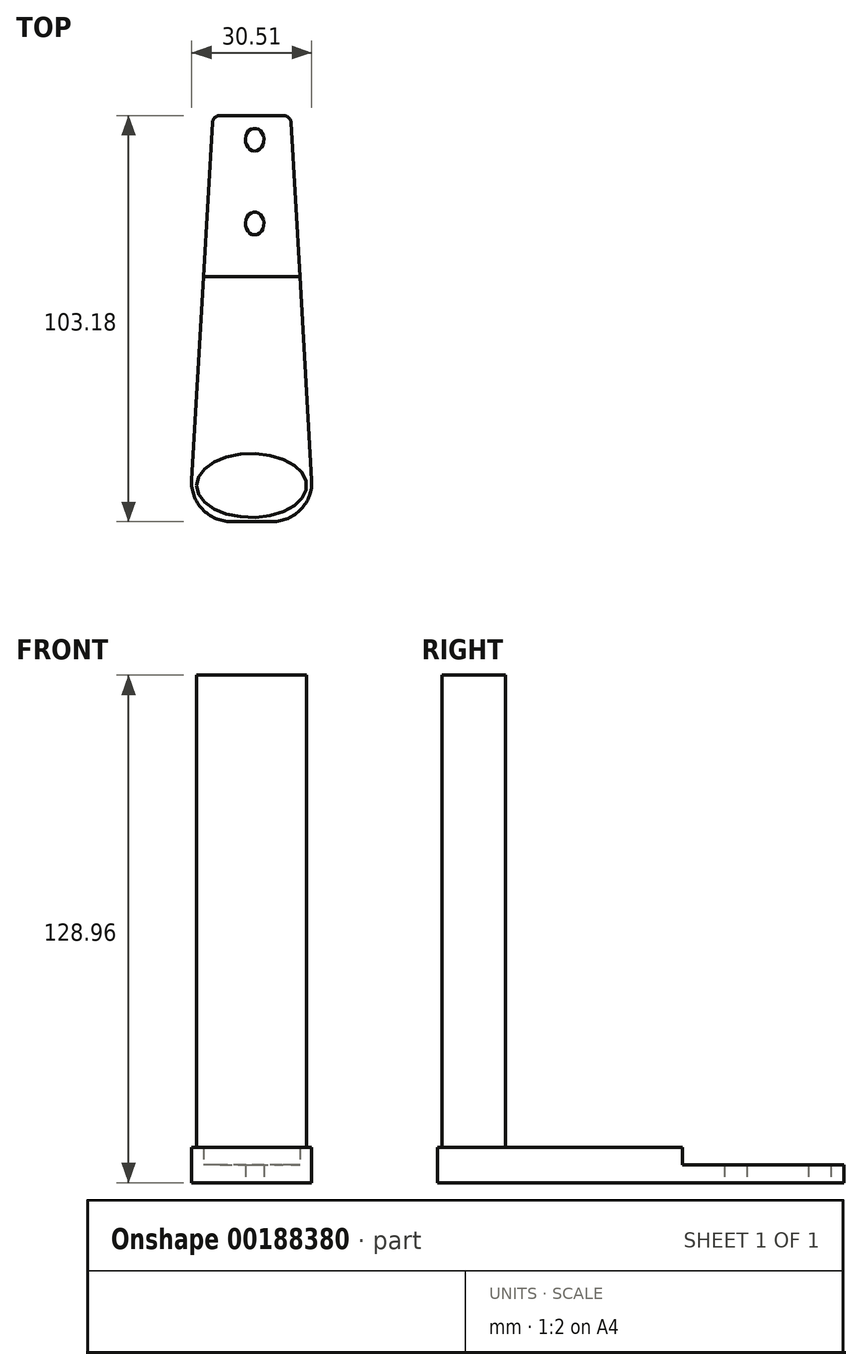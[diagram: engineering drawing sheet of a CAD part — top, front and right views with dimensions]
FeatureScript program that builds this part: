
annotation { "Feature Type Name" : "Feature", "Feature Type Description" : "" }
export const myFeature = defineFeature(function(context is Context, id is Id, definition is map)
    precondition{}
    {
        {
            var Q0;
            Q0=qCreatedBy(makeId("Top.planeOp"),FACE);
            var sketch = newSketch(context, id + "F0", { "sketchPlane" : qUnion([Q0])});
            skLineSegment(sketch, "E0", {"start": v(-8.74, 43.4) * mm, "end": v(7.26, 43.4) * mm});
            skLineSegment(sketch, "E1", {"start": v(-16.6, -59.78) * mm, "end": v(15.1, -59.78) * mm});
            skLineSegment(sketch, "E2", {"start": v(9.26, 41.52) * mm, "end": v(15.1, -59.78) * mm});
            skLineSegment(sketch, "E3", {"start": v(-10.74, 41.52) * mm, "end": v(-16.6, -59.78) * mm});
            skEllipse(sketch, "E4", {"center": v(0, 37.26) * mm, "majorRadius": 2.87 * mm, "minorRadius": 2.37 * mm, "majorAxis": v(0, -1)});
            skEllipse(sketch, "E5", {"center": v(0, 15.95) * mm, "majorRadius": 2.87 * mm, "minorRadius": 2.37 * mm, "majorAxis": v(0, -1)});
            skPoint(sketch, "E6.visualSharp", {"position": v(-10.63, 43.4) * mm});
            skArc(sketch, "E6.filletArc", {"start": v(-8.74, 43.4) * mm, "mid": v(-10.12, 42.86) * mm, "end": v(-10.74, 41.52) * mm});
            skPoint(sketch, "E7.visualSharp", {"position": v(9.15, 43.4) * mm});
            skArc(sketch, "E7.filletArc", {"start": v(9.26, 41.52) * mm, "mid": v(8.63, 42.86) * mm, "end": v(7.26, 43.4) * mm});
            skSolve(sketch);
        }
        {
            var Q0;
            Q0=makeQuery(id+"F0.imprint","IMPRINT",FACE,{"disambiguationData":[TD([[makeQuery(id+"F0.imprint","IMPRINT",EDGE,{"derivedFrom":sQuery(id+"F0.wireOp",EDGE,"E0")}),-1.0]])]});
            extrude(context, id + "F1", {"entities" : qUnion([Q0]), "depth" : 4.5 * mm});
        }
        {
            var Q0;
            Q0=qCreatedBy(makeId("Top.planeOp"),FACE);
            var sketch = newSketch(context, id + "F2", { "sketchPlane" : qUnion([Q0])});
            skLineSegment(sketch, "E8", {"start": v(-13, 2.41) * mm, "end": v(11.52, 2.41) * mm});
            skLineSegment(sketch, "E9", {"start": v(11.52, 2.41) * mm, "end": v(15.1, -59.78) * mm});
            skLineSegment(sketch, "E10", {"start": v(15.1, -59.78) * mm, "end": v(-16.6, -59.78) * mm});
            skLineSegment(sketch, "E11", {"start": v(-16.6, -59.78) * mm, "end": v(-13, 2.41) * mm});
            skSolve(sketch);
        }
        {
            var Q0;
            Q0 = qSketchRegion(id + "F2", true);
            extrude(context, id + "F3", {"entities" : qUnion([Q0]), "operationType" : NewBodyOperationType.ADD, "depth" : 8.96 * mm});
        }
        {
            var Q0;
            Q0=makeQuery(id+"F3.boolean.opBoolean","MERGE",EDGE,{"derivedFrom":[makeQuery(id+"F1.opExtrude","SWEPT_EDGE",EDGE,{"disambiguationData":[OSD([sQuery(id+"F0.wireOp",EDGE,"E1"),sQuery(id+"F0.wireOp",EDGE,"E2")])]}),makeQuery(id+"F3.opExtrude","SWEPT_EDGE",EDGE,{"disambiguationData":[OSD([sQuery(id+"F2.wireOp",EDGE,"E9"),sQuery(id+"F2.wireOp",EDGE,"E10")])]})]});
            fillet(context, id + "F4", {"entities" : qUnion([Q0]), "radius" : 10 * mm, "tangentPropagation" : true, "allowEdgeOverflow" : false});
        }
        {
            var Q0;
            Q0=makeQuery(id+"F3.boolean.opBoolean","MERGE",EDGE,{"derivedFrom":[makeQuery(id+"F1.opExtrude","SWEPT_EDGE",EDGE,{"disambiguationData":[OSD([sQuery(id+"F0.wireOp",EDGE,"E1"),sQuery(id+"F0.wireOp",EDGE,"E3")])]}),makeQuery(id+"F3.opExtrude","SWEPT_EDGE",EDGE,{"disambiguationData":[OSD([sQuery(id+"F2.wireOp",EDGE,"E10"),sQuery(id+"F2.wireOp",EDGE,"E11")])]})]});
            fillet(context, id + "F5", {"entities" : qUnion([Q0]), "radius" : 10 * mm, "tangentPropagation" : true, "allowEdgeOverflow" : false});
        }
        {
            var Q0;
            Q0=makeQuery(id+"F3.opExtrude","CAP_FACE",FACE,{"disambiguationData":[OSD([sQuery(id+"F2.wireOp",EDGE,"E8"),sQuery(id+"F2.wireOp",EDGE,"E9"),sQuery(id+"F2.wireOp",EDGE,"E10"),sQuery(id+"F2.wireOp",EDGE,"E11")])],"isStart":false});
            var sketch = newSketch(context, id + "F6", { "sketchPlane" : qUnion([Q0])});
            skEllipse(sketch, "E12", {"center": v(-0.77, -50.6) * mm, "majorRadius": 14 * mm, "minorRadius": 8.1 * mm, "majorAxis": v(-1, 0)});
            skSolve(sketch);
        }
        {
            var Q0;
            Q0 = qSketchRegion(id + "F6", true);
            extrude(context, id + "F7", {"entities" : qUnion([Q0]), "operationType" : NewBodyOperationType.ADD, "depth" : 120 * mm});
        }
    });
